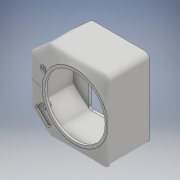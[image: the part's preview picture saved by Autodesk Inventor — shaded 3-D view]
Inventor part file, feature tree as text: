
AUTODESK INVENTOR PART (.ipt)
format: ipt  version: 2018 (Build 220112000, 112)  size: 4,144,640 bytes
history: native  units: mm
features: sketch x11, plane x6, extrude x5, fillet x5, loft x1, shell x1, hole x1, projected_geometry x1
ambient origin geometry x8: Origin, YZ Plane, XZ Plane, XY Plane, X Axis, Y Axis, Z Axis, Center Point
bodies: Body1 (feature_tree)
feature tree (31):
  sketch  "Sketch1"  dims[d0=-4.8mm d2=3.0mm]
  plane  "Work Plane1"
  sketch  "Sketch2"  dims[d3=15.0mm d4=15.0mm]
  plane  "Work Plane2"
  sketch  "Sketch3"  dims[d5=5.0mm d6=-30.0mm d7=-3.0mm]
  plane  "Work Plane3"
  sketch  "Sketch4"  dims[d8=-2.5mm d9=60.0mm]
  plane  "Work Plane4"
  sketch  "Sketch5"  dims[d32=4.8mm d53=0.0mm d54=90.0deg]
  plane  "Work Plane5"
  sketch  "Sketch6"  dims[d55=0.0mm d56=90.0deg d57=0.0mm d58=90.0deg]
  plane  "Work Plane6"
  loft  "Loft3"
  extrude  "Extrusion5"  Depth=15.0mm
  extrude  "Extrusion6"  [1 undecoded]
  shell  "Shell2"  Thickness=-3.0mm
  sketch  "Sketch14"  dims[d72=5.0mm]
  extrude  "Extrusion7"  Depth=60.0mm
  extrude  "Extrusion8"  TaperAngle=0.0deg  [1 undecoded]
  hole  "Hole1"  [1 undecoded]
  extrude  "Extrusion9"  TaperAngle=0.0deg  [1 undecoded]
  fillet  "Fillet2"  [1 undecoded]
  fillet  "Fillet3"  Radius=2.5mm
  fillet  "Fillet4"  Radius=2.5mm
  fillet  "Fillet5"  Radius=2.5mm
  fillet  "Fillet6"  Radius=2.5mm
  sketch  "Sketch10"  dims[d59=0.0mm d60=90.0deg d61=0.0mm d62=90.0deg d63=0.0mm d64=90.0deg d65=2.5mm d66=2.5mm d67=0.0mm d68=2.5mm d69=2.5mm d70=0.0mm]
  sketch  "Sketch13"  dims[d71=2.5mm]
  projected_geometry  "Projected Loop4"
  sketch  "Sketch15"  dims[d73=5.0mm]
  sketch  "Sketch19"  dims[d74=2.5mm d75=0.0mm d76=2.5mm d77=0.0mm d78=5.0mm d79=6.0mm d80=4.0mm d81=2.0mm d82=90.0deg d83=1.5mm d84=0.0mm d88=15.0mm d89=45.0deg d90=15.0mm d91=15.0mm d92=5.0mm d93=1.0mm d94=2.0mm d95=5.0mm d96=0.0mm d97=1.0mm d98=1.0mm d99=0.5mm d100=0.5mm d101=0.5mm]
note: 5 required parameter values undecoded (feature->parameter linkage not recoverable at this tier; creation-order binding heuristic only, values carry confidence <= 0.55)
